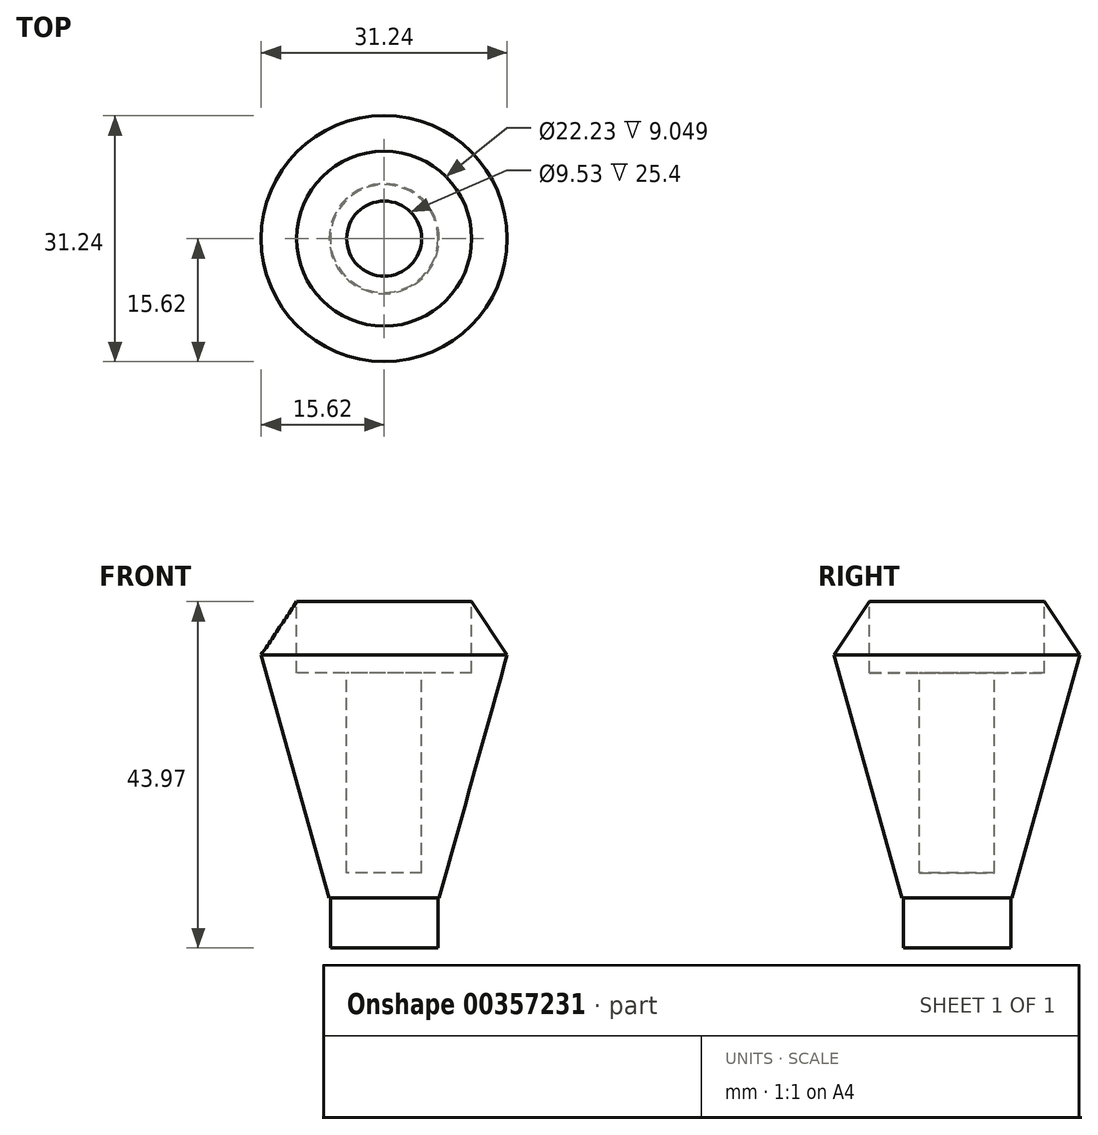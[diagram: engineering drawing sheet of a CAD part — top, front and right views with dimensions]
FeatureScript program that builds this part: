
annotation { "Feature Type Name" : "Feature", "Feature Type Description" : "" }
export const myFeature = defineFeature(function(context is Context, id is Id, definition is map)
    precondition{}
    {
        {
            var Q0;
            Q0=qCreatedBy(makeId("Top.planeOp"),FACE);
            var sketch = newSketch(context, id + "F0", { "sketchPlane" : qUnion([Q0])});
            skCircle(sketch, "E0", {"center": v(0, 0) * mm, "radius": 15.88 * mm});
            skSolve(sketch);
        }
        {
            var Q0;
            Q0 = qSketchRegion(id + "F0", true);
            extrude(context, id + "F1", {"entities" : qUnion([Q0]), "depth" : 31.75 * mm});
        }
        {
            var Q0;
            Q0=makeQuery(id+"F1.opExtrude","CAP_FACE",FACE,{"disambiguationData":[OSD([sQuery(id+"F0.wireOp",EDGE,"E0")])],"isStart":true});
            var sketch = newSketch(context, id + "F2", { "sketchPlane" : qUnion([Q0])});
            skCircle(sketch, "E1", {"center": v(0, 0) * mm, "radius": 6.84 * mm});
            skSolve(sketch);
        }
        {
            var Q0;
            Q0=makeQuery(id+"F2.imprint","IMPRINT",FACE,{"disambiguationData":[TD([[makeQuery(id+"F2.imprint","IMPRINT",EDGE,{"derivedFrom":sQuery(id+"F2.wireOp",EDGE,"E1")}),1.0]])]});
            extrude(context, id + "F3", {"entities" : qUnion([Q0]), "operationType" : NewBodyOperationType.ADD, "depth" : 6.35 * mm});
        }
        {
            var Q0;
            Q0=makeQuery(id+"F1.opExtrude","CAP_FACE",FACE,{"disambiguationData":[OSD([sQuery(id+"F0.wireOp",EDGE,"E0")])],"isStart":false});
            extrude(context, id + "F4", {"entities" : qUnion([Q0]), "operationType" : NewBodyOperationType.ADD, "depth" : 6.35 * mm});
        }
        {
            var Q0;
            Q0=makeQuery(id+"F4.opExtrude","CAP_FACE",FACE,{"disambiguationData":[OSD([sQuery(id+"F0.wireOp",EDGE,"E0")])],"isStart":false});
            var sketch = newSketch(context, id + "F5", { "sketchPlane" : qUnion([Q0])});
            skCircle(sketch, "E2", {"center": v(0, 0) * mm, "radius": 11.11 * mm});
            skSolve(sketch);
        }
        {
            var Q0;
            Q0=makeQuery(id+"F5.imprint","IMPRINT",FACE,{"disambiguationData":[TD([[makeQuery(id+"F5.imprint","IMPRINT",EDGE,{"derivedFrom":sQuery(id+"F5.wireOp",EDGE,"E2")}),1.0]])]});
            extrude(context, id + "F6", {"entities" : qUnion([Q0]), "operationType" : NewBodyOperationType.REMOVE, "oppositeDirection" : true, "depth" : 9.52 * mm});
        }
        {
            var Q0;
            Q0=makeQuery(id+"F6.boolean.opBoolean","COPY",FACE,{"derivedFrom":makeQuery(id+"F6.opExtrude","CAP_FACE",FACE,{"disambiguationData":[OSD([sQuery(id+"F5.wireOp",EDGE,"E2")])],"isStart":false})});
            var sketch = newSketch(context, id + "F7", { "sketchPlane" : qUnion([Q0])});
            skCircle(sketch, "E3", {"center": v(0, 0) * mm, "radius": 4.76 * mm});
            skSolve(sketch);
        }
        {
            var Q0;
            Q0=makeQuery(id+"F7.imprint","IMPRINT",FACE,{"disambiguationData":[TD([[makeQuery(id+"F7.imprint","IMPRINT",EDGE,{"derivedFrom":sQuery(id+"F7.wireOp",EDGE,"E3")}),1.0]])]});
            extrude(context, id + "F8", {"entities" : qUnion([Q0]), "operationType" : NewBodyOperationType.REMOVE, "oppositeDirection" : true, "depth" : 25.4 * mm});
        }
        {
            var Q0;
            Q0=makeQuery(id+"F1.opExtrude","CAP_EDGE",EDGE,{"disambiguationData":[OSD([sQuery(id+"F0.wireOp",EDGE,"E0")])],"isStart":true});
            chamfer(context, id + "F9", {"entities" : qUnion([Q0]), "chamferType" : ChamferType.TWO_OFFSETS, "width1" : 31.75 * mm, "oppositeDirection" : false, "width2" : 8.9 * mm, "tangentPropagation" : true});
        }
        {
            var Q0;
            Q0=makeQuery(id+"F4.opExtrude","CAP_EDGE",EDGE,{"disambiguationData":[OSD([sQuery(id+"F0.wireOp",EDGE,"E0")])],"isStart":false});
            chamfer(context, id + "F10", {"entities" : qUnion([Q0]), "chamferType" : ChamferType.TWO_OFFSETS, "width1" : 5.08 * mm, "oppositeDirection" : false, "width2" : 7.62 * mm, "tangentPropagation" : true});
        }
    });
